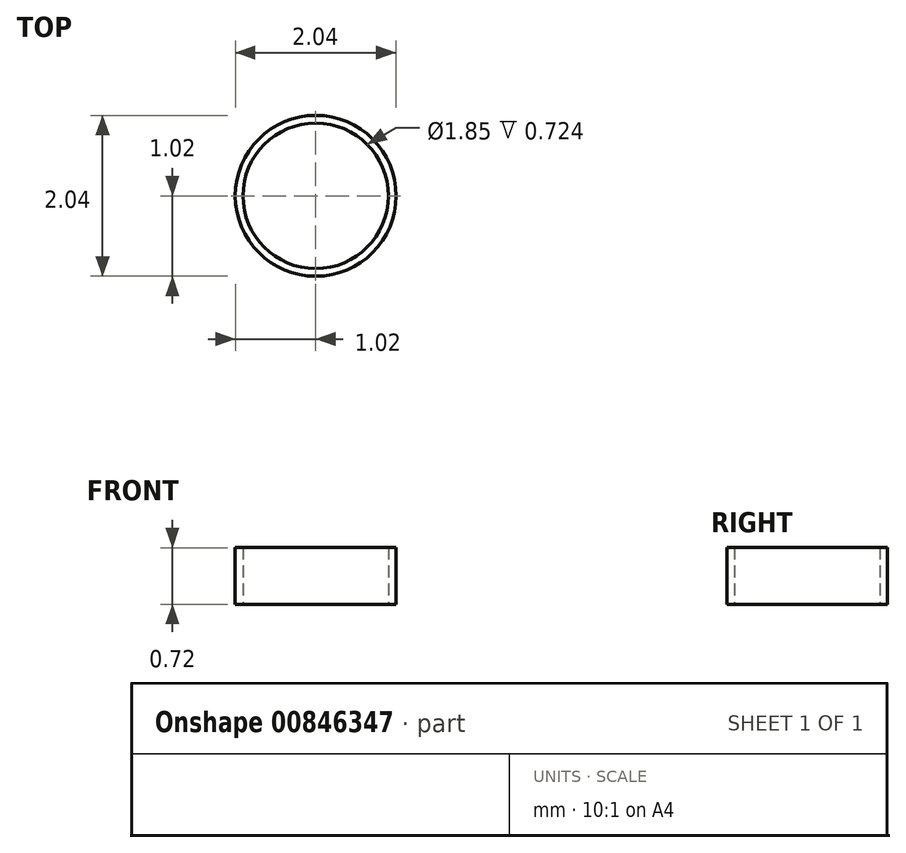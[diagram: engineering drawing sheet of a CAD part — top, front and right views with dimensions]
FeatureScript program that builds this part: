
annotation { "Feature Type Name" : "Feature", "Feature Type Description" : "" }
export const myFeature = defineFeature(function(context is Context, id is Id, definition is map)
    precondition{}
    {
        {
            var Q0;
            Q0=qCreatedBy(makeId("Top.planeOp"),FACE);
            var sketch = newSketch(context, id + "F0", { "sketchPlane" : qUnion([Q0])});
            skCircle(sketch, "E0", {"center": v(0, 0) * mm, "radius": 1.02 * mm});
            skSolve(sketch);
        }
        {
            var Q0;
            Q0 = qSketchRegion(id + "F0", true);
            extrude(context, id + "F1", {"entities" : qUnion([Q0]), "depth" : 0.22 * mm, "offsetDistance" : 25.4 * mm});
        }
        {
            var Q0;
            Q0=qCreatedBy(makeId("Top.planeOp"),FACE);
            var sketch = newSketch(context, id + "F2", { "sketchPlane" : qUnion([Q0])});
            skCircle(sketch, "E1", {"center": v(0, 0) * mm, "radius": 0.92 * mm});
            skSolve(sketch);
        }
        {
            var Q0;
            Q0 = qSketchRegion(id + "F2", true);
            var Q1;
            Q1=makeQuery(id+"F1.opExtrude","CAP_FACE",FACE,{"disambiguationData":[OSD([sQuery(id+"F0.wireOp",EDGE,"E0")])],"isStart":false});
            extrude(context, id + "F3", {"entities" : qUnion([Q0, Q1]), "operationType" : NewBodyOperationType.REMOVE, "depth" : 0.42 * mm, "offsetDistance" : 25.4 * mm});
        }
        {
            var Q0;
            Q0=makeQuery(id+"F1.opExtrude","CAP_FACE",FACE,{"disambiguationData":[OSD([sQuery(id+"F0.wireOp",EDGE,"E0")])],"isStart":false});
            var sketch = newSketch(context, id + "F4", { "sketchPlane" : qUnion([Q0])});
            skSolve(sketch);
        }
        {
            var Q0;
            {var subQ0=sQuery(id+"F0.wireOp",EDGE,"E0");Q0=makeQuery(id+"F4.imprint","IMPRINT",FACE,{"disambiguationData":[TD([[makeQuery(id+"F4.imprint","IMPRINT",EDGE,{"derivedFrom":makeQuery(id+"F3.boolean.opBoolean","INTERSECT",EDGE,{"derivedFrom":[makeQuery(id+"F1.opExtrude","CAP_FACE",FACE,{"disambiguationData":[OSD([subQ0])],"isStart":false}),makeQuery(id+"F3.opExtrude","CAP_FACE",FACE,{"disambiguationData":[OSD([subQ0])],"isStart":true})]})}),1.0]])]});}
            var Q1;
            {var subQ0=sQuery(id+"F0.wireOp",EDGE,"E0");Q1=makeQuery(id+"F4.imprint","IMPRINT",FACE,{"disambiguationData":[TD([[makeQuery(id+"F4.imprint","IMPRINT",EDGE,{"derivedFrom":makeQuery(id+"F1.opExtrude","CAP_EDGE",EDGE,{"disambiguationData":[OSD([subQ0])],"isStart":false})}),1.0]])]});}
            extrude(context, id + "F5", {"entities" : qUnion([Q0, Q1]), "operationType" : NewBodyOperationType.ADD, "depth" : 0.5 * mm, "offsetDistance" : 25.4 * mm});
        }
        {
            var Q0;
            Q0=makeQuery(id+"F5.opExtrude","CAP_FACE",FACE,{"disambiguationData":[OSD([sQuery(id+"F0.wireOp",EDGE,"E0")])],"isStart":false});
            var sketch = newSketch(context, id + "F6", { "sketchPlane" : qUnion([Q0])});
            skCircle(sketch, "E2", {"center": v(0, 0) * mm, "radius": 0.24 * mm});
            skSolve(sketch);
        }
        {
            var Q0;
            Q0 = qSketchRegion(id + "F6", true);
            extrude(context, id + "F7", {"entities" : qUnion([Q0]), "operationType" : NewBodyOperationType.REMOVE, "oppositeDirection" : true, "depth" : 25.4 * mm, "offsetDistance" : 25.4 * mm});
        }
    });
